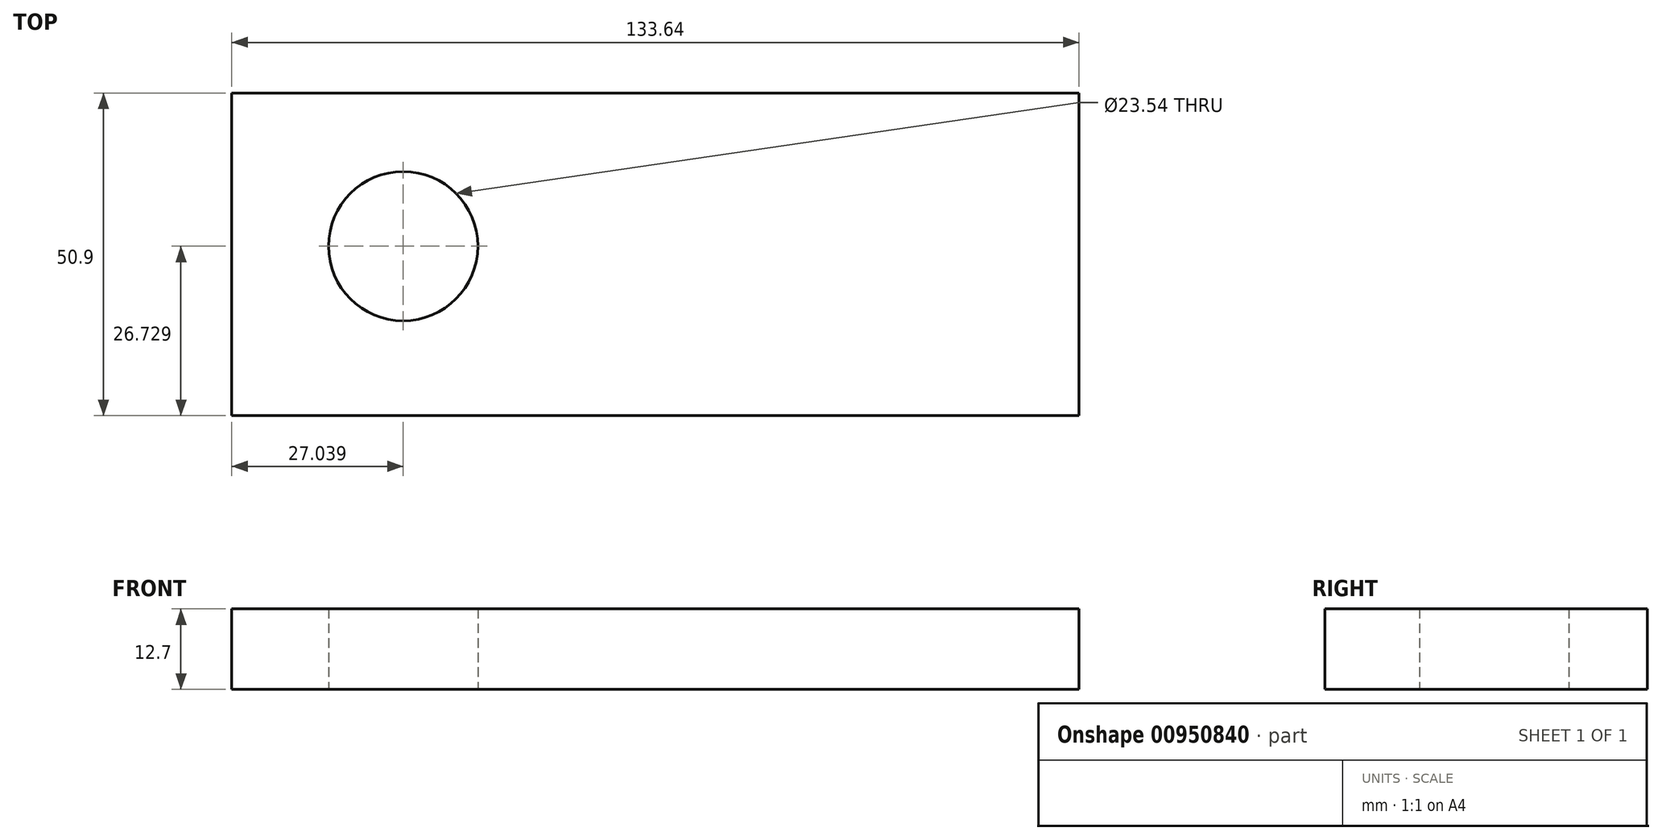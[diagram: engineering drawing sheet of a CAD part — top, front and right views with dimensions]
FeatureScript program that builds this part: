
annotation { "Feature Type Name" : "Feature", "Feature Type Description" : "" }
export const myFeature = defineFeature(function(context is Context, id is Id, definition is map)
    precondition{}
    {
        {
            var Q0;
            Q0=qCreatedBy(makeId("Top.planeOp"),FACE);
            var sketch = newSketch(context, id + "F0", { "sketchPlane" : qUnion([Q0])});
            skLineSegment(sketch, "E0.bottom", {"start": v(0, 0) * mm, "end": v(133.64, 0) * mm});
            skLineSegment(sketch, "E0.top", {"start": v(0, -50.9) * mm, "end": v(133.64, -50.9) * mm});
            skLineSegment(sketch, "E0.left", {"start": v(0, 0) * mm, "end": v(0, -50.9) * mm});
            skLineSegment(sketch, "E0.right", {"start": v(133.64, 0) * mm, "end": v(133.64, -50.9) * mm});
            skCircle(sketch, "E1", {"center": v(27.04, -24.17) * mm, "radius": 11.77 * mm});
            skSolve(sketch);
        }
        {
            var Q0;
            Q0 = qSketchRegion(id + "F0sSOuPnOdT6Weg_0", true);
            var Q1;
            Q1 = qSketchRegion(id + "F0", true);
            extrude(context, id + "F1", {"entities" : qUnion([Q0, Q1]), "depth" : 12.7 * mm, "offsetDistance" : 25.4 * mm});
        }
    });
